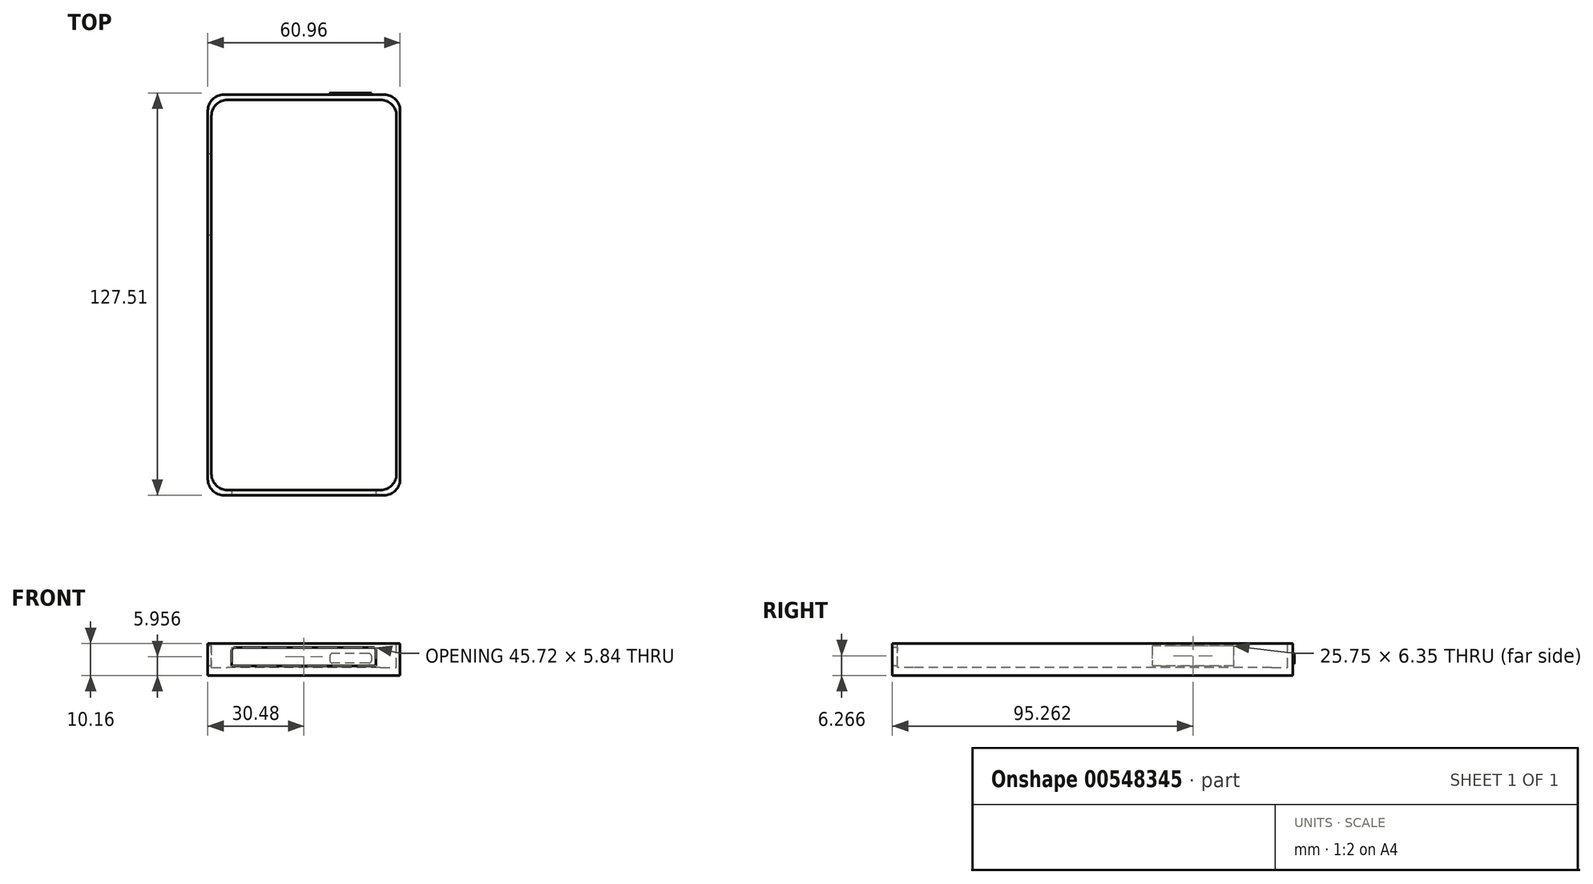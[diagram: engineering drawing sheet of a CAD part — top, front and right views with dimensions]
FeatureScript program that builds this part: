
annotation { "Feature Type Name" : "Feature", "Feature Type Description" : "" }
export const myFeature = defineFeature(function(context is Context, id is Id, definition is map)
    precondition{}
    {
        {
            var Q0;
            Q0=qCreatedBy(makeId("Top.planeOp"),FACE);
            var sketch = newSketch(context, id + "F0", { "sketchPlane" : qUnion([Q0])});
            skLineSegment(sketch, "E0.bottom", {"start": v(30.48, 63.5) * mm, "end": v(-30.48, 63.5) * mm});
            skLineSegment(sketch, "E0.top", {"start": v(30.48, -63.5) * mm, "end": v(-30.48, -63.5) * mm});
            skLineSegment(sketch, "E0.left", {"start": v(30.48, 63.5) * mm, "end": v(30.48, -63.5) * mm});
            skLineSegment(sketch, "E0.right", {"start": v(-30.48, 63.5) * mm, "end": v(-30.48, -63.5) * mm});
            skPoint(sketch, "E0.middle", {"position": v(0, 0) * mm});
            skSolve(sketch);
        }
        {
            var Q0;
            Q0 = qSketchRegion(id + "F0", true);
            extrude(context, id + "F1", {"entities" : qUnion([Q0]), "depth" : 10.16 * mm, "offsetDistance" : 25.4 * mm});
        }
        {
            var Q0;
            Q0=makeQuery(id+"F1.opExtrude","CAP_FACE",FACE,{"disambiguationData":[OSD([sQuery(id+"F0.wireOp",EDGE,"E0.bottom"),sQuery(id+"F0.wireOp",EDGE,"E0.top"),sQuery(id+"F0.wireOp",EDGE,"E0.left"),sQuery(id+"F0.wireOp",EDGE,"E0.right")])],"isStart":false});
            var sketch = newSketch(context, id + "F2", { "sketchPlane" : qUnion([Q0])});
            skLineSegment(sketch, "E1.bottom", {"start": v(29.34, 61.85) * mm, "end": v(-29.34, 61.85) * mm});
            skLineSegment(sketch, "E1.top", {"start": v(29.34, -61.85) * mm, "end": v(-29.34, -61.85) * mm});
            skLineSegment(sketch, "E1.left", {"start": v(29.34, 61.85) * mm, "end": v(29.34, -61.85) * mm});
            skLineSegment(sketch, "E1.right", {"start": v(-29.34, 61.85) * mm, "end": v(-29.34, -61.85) * mm});
            skPoint(sketch, "E1.middle", {"position": v(0, 0) * mm});
            skSolve(sketch);
        }
        {
            var Q0;
            Q0=makeQuery(id+"F2.imprint","IMPRINT",FACE,{"disambiguationData":[TD([[makeQuery(id+"F2.imprint","IMPRINT",EDGE,{"derivedFrom":sQuery(id+"F2.wireOp",EDGE,"E1.bottom")}),1.0]])]});
            extrude(context, id + "F3", {"entities" : qUnion([Q0]), "operationType" : NewBodyOperationType.REMOVE, "oppositeDirection" : true, "depth" : 7.62 * mm, "offsetDistance" : 25.4 * mm});
        }
        {
            var Q0;
            Q0=makeQuery(id+"F3.boolean.opBoolean","COPY",EDGE,{"derivedFrom":makeQuery(id+"F3.opExtrude","SWEPT_EDGE",EDGE,{"disambiguationData":[OSD([sQuery(id+"F2.wireOp",EDGE,"E1.bottom"),sQuery(id+"F2.wireOp",EDGE,"E1.right")])]})});
            fillet(context, id + "F4", {"entities" : qUnion([Q0]), "radius" : 5.08 * mm, "tangentPropagation" : true, "allowEdgeOverflow" : false});
        }
        {
            var Q0;
            Q0=makeQuery(id+"F3.boolean.opBoolean","COPY",EDGE,{"derivedFrom":makeQuery(id+"F3.opExtrude","SWEPT_EDGE",EDGE,{"disambiguationData":[OSD([sQuery(id+"F2.wireOp",EDGE,"E1.bottom"),sQuery(id+"F2.wireOp",EDGE,"E1.left")])]})});
            var Q1;
            Q1=makeQuery(id+"F3.boolean.opBoolean","COPY",EDGE,{"derivedFrom":makeQuery(id+"F3.opExtrude","SWEPT_EDGE",EDGE,{"disambiguationData":[OSD([sQuery(id+"F2.wireOp",EDGE,"E1.top"),sQuery(id+"F2.wireOp",EDGE,"E1.left")])]})});
            var Q2;
            Q2=makeQuery(id+"F3.boolean.opBoolean","COPY",EDGE,{"derivedFrom":makeQuery(id+"F3.opExtrude","SWEPT_EDGE",EDGE,{"disambiguationData":[OSD([sQuery(id+"F2.wireOp",EDGE,"E1.top"),sQuery(id+"F2.wireOp",EDGE,"E1.right")])]})});
            var Q3;
            Q3=makeQuery(id+"F1.opExtrude","SWEPT_EDGE",EDGE,{"disambiguationData":[OSD([sQuery(id+"F0.wireOp",EDGE,"E0.bottom"),sQuery(id+"F0.wireOp",EDGE,"E0.left")])]});
            var Q4;
            Q4=makeQuery(id+"F1.opExtrude","SWEPT_EDGE",EDGE,{"disambiguationData":[OSD([sQuery(id+"F0.wireOp",EDGE,"E0.bottom"),sQuery(id+"F0.wireOp",EDGE,"E0.right")])]});
            var Q5;
            Q5=makeQuery(id+"F1.opExtrude","SWEPT_EDGE",EDGE,{"disambiguationData":[OSD([sQuery(id+"F0.wireOp",EDGE,"E0.top"),sQuery(id+"F0.wireOp",EDGE,"E0.right")])]});
            var Q6;
            Q6=makeQuery(id+"F1.opExtrude","SWEPT_EDGE",EDGE,{"disambiguationData":[OSD([sQuery(id+"F0.wireOp",EDGE,"E0.top"),sQuery(id+"F0.wireOp",EDGE,"E0.left")])]});
            fillet(context, id + "F5", {"entities" : qUnion([Q0, Q1, Q2, Q3, Q4, Q5, Q6]), "radius" : 5.08 * mm, "tangentPropagation" : true, "allowEdgeOverflow" : false});
        }
        {
            var Q0;
            Q0=makeQuery(id+"F1.opExtrude","SWEPT_FACE",FACE,{"disambiguationData":[OSD([sQuery(id+"F0.wireOp",EDGE,"E0.top")])]});
            var sketch = newSketch(context, id + "F6", { "sketchPlane" : qUnion([Q0])});
            skLineSegment(sketch, "E2.bottom", {"start": v(-22.86, 8.88) * mm, "end": v(22.86, 8.88) * mm});
            skLineSegment(sketch, "E2.top", {"start": v(-22.86, 3.04) * mm, "end": v(22.86, 3.04) * mm});
            skLineSegment(sketch, "E2.left", {"start": v(-22.86, 8.88) * mm, "end": v(-22.86, 3.04) * mm});
            skLineSegment(sketch, "E2.right", {"start": v(22.86, 8.88) * mm, "end": v(22.86, 3.04) * mm});
            skPoint(sketch, "E2.middle", {"position": v(0, 5.96) * mm});
            skSolve(sketch);
        }
        {
            var Q0;
            Q0=makeQuery(id+"F6.imprint","IMPRINT",FACE,{"disambiguationData":[TD([[makeQuery(id+"F6.imprint","IMPRINT",EDGE,{"derivedFrom":sQuery(id+"F6.wireOp",EDGE,"E2.bottom")}),-1.0]])]});
            extrude(context, id + "F7", {"entities" : qUnion([Q0]), "operationType" : NewBodyOperationType.REMOVE, "oppositeDirection" : true, "depth" : 25.4 * mm, "offsetDistance" : 25.4 * mm});
        }
        {
            var Q0;
            Q0=makeQuery(id+"F7.boolean.opBoolean","COPY",EDGE,{"derivedFrom":makeQuery(id+"F7.opExtrude","SWEPT_EDGE",EDGE,{"disambiguationData":[OSD([sQuery(id+"F6.wireOp",EDGE,"E2.bottom"),sQuery(id+"F6.wireOp",EDGE,"E2.left")])]})});
            var Q1;
            Q1=makeQuery(id+"F7.boolean.opBoolean","COPY",EDGE,{"derivedFrom":makeQuery(id+"F7.opExtrude","SWEPT_EDGE",EDGE,{"disambiguationData":[OSD([sQuery(id+"F6.wireOp",EDGE,"E2.bottom"),sQuery(id+"F6.wireOp",EDGE,"E2.right")])]})});
            fillet(context, id + "F8", {"entities" : qUnion([Q0, Q1]), "radius" : 1.02 * mm, "tangentPropagation" : true, "allowEdgeOverflow" : false});
        }
        {
            var Q0;
            Q0=makeQuery(id+"F1.opExtrude","SWEPT_FACE",FACE,{"disambiguationData":[OSD([sQuery(id+"F0.wireOp",EDGE,"E0.right")])]});
            var sketch = newSketch(context, id + "F9", { "sketchPlane" : qUnion([Q0])});
            skLineSegment(sketch, "E3.bottom", {"start": v(-44.64, 9.44) * mm, "end": v(-18.89, 9.44) * mm});
            skLineSegment(sketch, "E3.top", {"start": v(-44.64, 3.1) * mm, "end": v(-18.89, 3.1) * mm});
            skLineSegment(sketch, "E3.left", {"start": v(-44.64, 9.44) * mm, "end": v(-44.64, 3.1) * mm});
            skLineSegment(sketch, "E3.right", {"start": v(-18.89, 9.44) * mm, "end": v(-18.89, 3.1) * mm});
            skPoint(sketch, "E3.middle", {"position": v(-31.76, 6.27) * mm});
            skSolve(sketch);
        }
        {
            var Q0;
            Q0=makeQuery(id+"F9.imprint","IMPRINT",FACE,{"disambiguationData":[TD([[makeQuery(id+"F9.imprint","IMPRINT",EDGE,{"derivedFrom":sQuery(id+"F9.wireOp",EDGE,"E3.bottom")}),-1.0]])]});
            extrude(context, id + "F10", {"entities" : qUnion([Q0]), "operationType" : NewBodyOperationType.REMOVE, "oppositeDirection" : true, "depth" : 25.4 * mm, "offsetDistance" : 25.4 * mm});
        }
        {
            var Q0;
            Q0=makeQuery(id+"F1.opExtrude","SWEPT_FACE",FACE,{"disambiguationData":[OSD([sQuery(id+"F0.wireOp",EDGE,"E0.bottom")])]});
            var sketch = newSketch(context, id + "F11", { "sketchPlane" : qUnion([Q0])});
            skLineSegment(sketch, "E4.bottom", {"start": v(-21.36, 6.95) * mm, "end": v(-8.22, 6.95) * mm});
            skLineSegment(sketch, "E4.top", {"start": v(-21.36, 3.92) * mm, "end": v(-8.22, 3.92) * mm});
            skLineSegment(sketch, "E4.left", {"start": v(-21.36, 6.95) * mm, "end": v(-21.36, 3.92) * mm});
            skLineSegment(sketch, "E4.right", {"start": v(-8.22, 6.95) * mm, "end": v(-8.22, 3.92) * mm});
            skPoint(sketch, "E4.middle", {"position": v(-14.79, 5.44) * mm});
            skSolve(sketch);
        }
        {
            var Q0;
            Q0=makeQuery(id+"F11.imprint","IMPRINT",FACE,{"disambiguationData":[TD([[makeQuery(id+"F11.imprint","IMPRINT",EDGE,{"derivedFrom":sQuery(id+"F11.wireOp",EDGE,"E4.bottom")}),-1.0]])]});
            extrude(context, id + "F12", {"entities" : qUnion([Q0]), "operationType" : NewBodyOperationType.ADD, "depth" : 0.5 * mm, "offsetDistance" : 25.4 * mm});
        }
        {
            var Q0;
            Q0=makeQuery(id+"F12.opExtrude","SWEPT_EDGE",EDGE,{"disambiguationData":[OSD([sQuery(id+"F11.wireOp",EDGE,"E4.top"),sQuery(id+"F11.wireOp",EDGE,"E4.right")])]});
            var Q1;
            Q1=makeQuery(id+"F12.opExtrude","SWEPT_EDGE",EDGE,{"disambiguationData":[OSD([sQuery(id+"F11.wireOp",EDGE,"E4.bottom"),sQuery(id+"F11.wireOp",EDGE,"E4.right")])]});
            var Q2;
            Q2=makeQuery(id+"F12.opExtrude","SWEPT_EDGE",EDGE,{"disambiguationData":[OSD([sQuery(id+"F11.wireOp",EDGE,"E4.top"),sQuery(id+"F11.wireOp",EDGE,"E4.left")])]});
            var Q3;
            Q3=makeQuery(id+"F12.opExtrude","SWEPT_EDGE",EDGE,{"disambiguationData":[OSD([sQuery(id+"F11.wireOp",EDGE,"E4.bottom"),sQuery(id+"F11.wireOp",EDGE,"E4.left")])]});
            fillet(context, id + "F13", {"entities" : qUnion([Q0, Q1, Q2, Q3]), "radius" : 0.76 * mm, "tangentPropagation" : true, "allowEdgeOverflow" : false});
        }
    });
